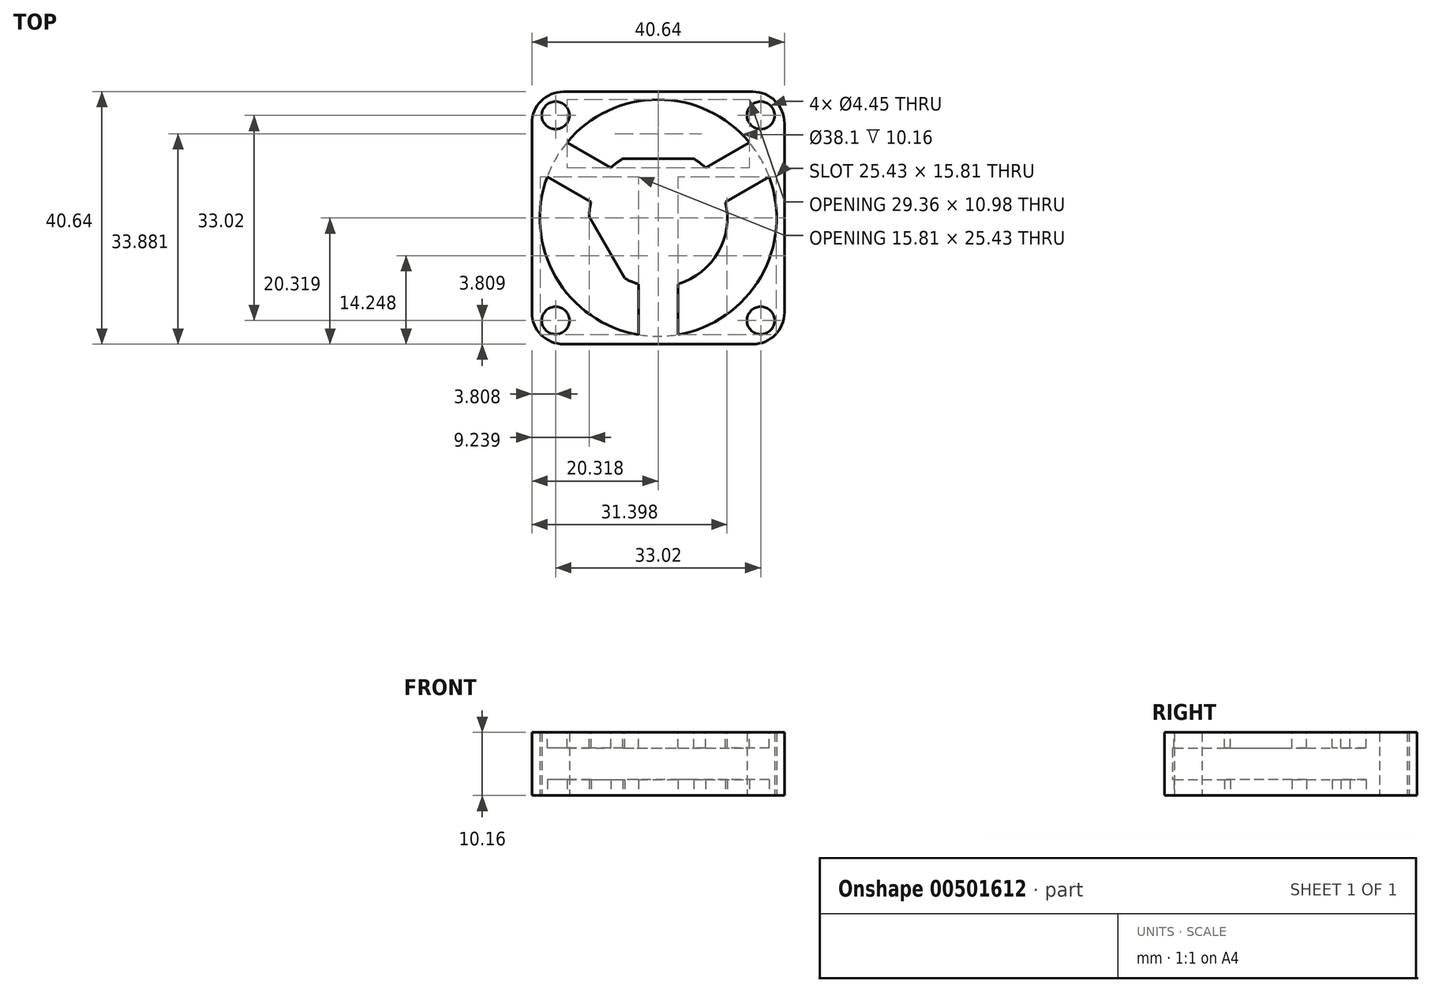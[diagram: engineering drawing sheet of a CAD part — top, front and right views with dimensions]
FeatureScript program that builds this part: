
annotation { "Feature Type Name" : "Feature", "Feature Type Description" : "" }
export const myFeature = defineFeature(function(context is Context, id is Id, definition is map)
    precondition{}
    {
        {
            var Q0;
            Q0=qCreatedBy(makeId("Top.planeOp"),FACE);
            var sketch = newSketch(context, id + "F0", { "sketchPlane" : qUnion([Q0])});
            skLineSegment(sketch, "E0.bottom", {"start": v(-69.1, 68.37) * mm, "end": v(-28.46, 68.37) * mm});
            skLineSegment(sketch, "E0.top", {"start": v(-69.1, 27.73) * mm, "end": v(-28.46, 27.73) * mm});
            skLineSegment(sketch, "E0.left", {"start": v(-69.1, 68.37) * mm, "end": v(-69.1, 27.73) * mm});
            skLineSegment(sketch, "E0.right", {"start": v(-28.46, 68.37) * mm, "end": v(-28.46, 27.73) * mm});
            skCircle(sketch, "E1", {"center": v(-65.3, 64.56) * mm, "radius": 2.22 * mm});
            skCircle(sketch, "E2", {"center": v(-32.27, 64.56) * mm, "radius": 2.22 * mm});
            skCircle(sketch, "E3", {"center": v(-65.3, 31.54) * mm, "radius": 2.22 * mm});
            skCircle(sketch, "E4", {"center": v(-32.27, 31.54) * mm, "radius": 2.22 * mm});
            skCircle(sketch, "E5", {"center": v(-48.78, 48.05) * mm, "radius": 19.05 * mm});
            skPoint(sketch, "E5.centerSnap0", {"position": v(-48.78, 68.37) * mm});
            skPoint(sketch, "E5.centerSnap1", {"position": v(-69.1, 48.05) * mm});
            skSolve(sketch);
        }
        {
            var Q0;
            Q0 = qSketchRegion(id + "F0", true);
            extrude(context, id + "F1", {"entities" : qUnion([Q0]), "depth" : 10.16 * mm});
        }
        {
            var Q0;
            Q0=makeQuery(id+"F1.opExtrude","CAP_FACE",FACE,{"disambiguationData":[OSD([sQuery(id+"F0.wireOp",EDGE,"E0.bottom"),sQuery(id+"F0.wireOp",EDGE,"E0.top"),sQuery(id+"F0.wireOp",EDGE,"E0.left"),sQuery(id+"F0.wireOp",EDGE,"E0.right"),sQuery(id+"F0.wireOp",EDGE,"E1"),sQuery(id+"F0.wireOp",EDGE,"E2"),sQuery(id+"F0.wireOp",EDGE,"E3"),sQuery(id+"F0.wireOp",EDGE,"E4"),sQuery(id+"F0.wireOp",EDGE,"E5")])],"isStart":true});
            var sketch = newSketch(context, id + "F2", { "sketchPlane" : qUnion([Q0])});
            skPoint(sketch, "E6", {"position": v(-48.78, -48.05) * mm});
            skCircle(sketch, "E7", {"center": v(-48.78, -48.05) * mm, "radius": 11.11 * mm});
            skCircle(sketch, "E8", {"center": v(-48.78, -48.05) * mm, "radius": 19.05 * mm});
            skPoint(sketch, "E9.0.midPoint", {"position": v(-48.78, -67.1) * mm});
            skCircle(sketch, "E10.cCircle", {"center": v(-48.78, -48.05) * mm, "radius": 9.53 * mm, "construction": true});
            skLineSegment(sketch, "E10.0", {"start": v(-32.28, -57.57) * mm, "end": v(-65.28, -57.57) * mm});
            skLineSegment(sketch, "E10.1", {"start": v(-65.28, -57.57) * mm, "end": v(-48.78, -29) * mm});
            skLineSegment(sketch, "E10.2", {"start": v(-48.78, -29) * mm, "end": v(-32.28, -57.57) * mm});
            skPoint(sketch, "E10.0.midPoint", {"position": v(-48.78, -57.57) * mm});
            skLineSegment(sketch, "E11", {"start": v(-65.28, -57.57) * mm, "end": v(-48.78, -48.05) * mm});
            skLineSegment(sketch, "E12", {"start": v(-32.28, -57.57) * mm, "end": v(-48.78, -48.05) * mm});
            skLineSegment(sketch, "E13", {"start": v(-48.78, -29) * mm, "end": v(-48.78, -48.05) * mm});
            skLineSegment(sketch, "E14", {"start": v(-65.28, -57.57) * mm, "end": v(-63.7, -60.32) * mm});
            skLineSegment(sketch, "E15", {"start": v(-63.7, -60.32) * mm, "end": v(-47.2, -50.8) * mm});
            skLineSegment(sketch, "E16", {"start": v(-47.2, -50.8) * mm, "end": v(-50.37, -45.3) * mm});
            skLineSegment(sketch, "E17", {"start": v(-50.37, -45.3) * mm, "end": v(-66.87, -54.82) * mm});
            skLineSegment(sketch, "E18", {"start": v(-66.87, -54.82) * mm, "end": v(-65.28, -57.57) * mm});
            skLineSegment(sketch, "E19", {"start": v(-32.28, -57.57) * mm, "end": v(-30.7, -54.82) * mm});
            skLineSegment(sketch, "E20", {"start": v(-30.7, -54.82) * mm, "end": v(-47.2, -45.3) * mm});
            skLineSegment(sketch, "E21", {"start": v(-47.2, -45.3) * mm, "end": v(-48.78, -48.05) * mm});
            skLineSegment(sketch, "E22", {"start": v(-48.78, -48.05) * mm, "end": v(-50.37, -50.8) * mm});
            skLineSegment(sketch, "E23", {"start": v(-50.37, -50.8) * mm, "end": v(-33.87, -60.32) * mm});
            skLineSegment(sketch, "E24", {"start": v(-33.87, -60.32) * mm, "end": v(-32.28, -57.57) * mm});
            skLineSegment(sketch, "E25", {"start": v(-48.78, -29) * mm, "end": v(-45.6, -29) * mm});
            skLineSegment(sketch, "E26", {"start": v(-45.6, -29) * mm, "end": v(-45.6, -48.05) * mm});
            skLineSegment(sketch, "E27", {"start": v(-45.6, -48.05) * mm, "end": v(-48.78, -48.05) * mm});
            skLineSegment(sketch, "E28", {"start": v(-48.78, -48.05) * mm, "end": v(-51.96, -48.05) * mm});
            skLineSegment(sketch, "E29", {"start": v(-51.96, -48.05) * mm, "end": v(-51.96, -29) * mm});
            skLineSegment(sketch, "E30", {"start": v(-51.96, -29) * mm, "end": v(-48.78, -29) * mm});
            skSolve(sketch);
        }
        {
            var Q0;
            {var subQ0=sQuery(id+"F2.wireOp",EDGE,"E17");var subQ1=sQuery(id+"F2.wireOp",EDGE,"E7");var subQ2=makeQuery(id+"F2.imprint","INTERSECT",VERTEX,{"derivedFrom":[subQ1,subQ0]});Q0=makeQuery(id+"F2.imprint","IMPRINT",FACE,{"disambiguationData":[TD([[makeQuery(id+"F2.imprint","IMPRINT",EDGE,{"disambiguationData":[TD([[subQ2,-1.0]])],"derivedFrom":subQ1}),-1.0]])]});}
            var Q1;
            {var subQ1=sQuery(id+"F2.wireOp",EDGE,"E8");var subQ3=sQuery(id+"F2.wireOp",EDGE,"E15");var subQ4=makeQuery(id+"F2.imprint","INTERSECT",VERTEX,{"derivedFrom":[subQ1,subQ3]});Q1=makeQuery(id+"F2.imprint","IMPRINT",FACE,{"disambiguationData":[TD([[makeQuery(id+"F2.imprint","IMPRINT",EDGE,{"disambiguationData":[TD([[subQ4,-1.0]])],"derivedFrom":subQ3}),1.0]])]});}
            var Q2;
            {var subQ0=sQuery(id+"F2.wireOp",EDGE,"E11");var subQ1=sQuery(id+"F2.wireOp",EDGE,"E7");var subQ2=makeQuery(id+"F2.imprint","INTERSECT",VERTEX,{"derivedFrom":[subQ1,subQ0]});Q2=makeQuery(id+"F2.imprint","IMPRINT",FACE,{"disambiguationData":[TD([[makeQuery(id+"F2.imprint","IMPRINT",EDGE,{"disambiguationData":[TD([[subQ2,-1.0]])],"derivedFrom":subQ1}),-1.0]])]});}
            var Q3;
            {var subQ1=sQuery(id+"F2.wireOp",EDGE,"E8");var subQ3=sQuery(id+"F2.wireOp",EDGE,"E17");var subQ4=makeQuery(id+"F2.imprint","INTERSECT",VERTEX,{"derivedFrom":[subQ1,subQ3]});Q3=makeQuery(id+"F2.imprint","IMPRINT",FACE,{"disambiguationData":[TD([[makeQuery(id+"F2.imprint","IMPRINT",EDGE,{"disambiguationData":[TD([[subQ4,1.0]])],"derivedFrom":subQ3}),1.0]])]});}
            var Q4;
            {var subQ5=sQuery(id+"F2.wireOp",EDGE,"E28");Q4=makeQuery(id+"F2.imprint","IMPRINT",FACE,{"disambiguationData":[TD([[makeQuery(id+"F2.imprint","IMPRINT",EDGE,{"derivedFrom":subQ5}),1.0]])]});}
            var Q5;
            {var subQ0=sQuery(id+"F2.wireOp",EDGE,"E22");Q5=makeQuery(id+"F2.imprint","IMPRINT",FACE,{"disambiguationData":[TD([[makeQuery(id+"F2.imprint","IMPRINT",EDGE,{"derivedFrom":subQ0}),-1.0]])]});}
            var Q6;
            {var subQ0=sQuery(id+"F2.wireOp",EDGE,"E15");var subQ1=sQuery(id+"F2.wireOp",EDGE,"E7");var subQ2=makeQuery(id+"F2.imprint","INTERSECT",VERTEX,{"derivedFrom":[subQ1,subQ0]});Q6=makeQuery(id+"F2.imprint","IMPRINT",FACE,{"disambiguationData":[TD([[makeQuery(id+"F2.imprint","IMPRINT",EDGE,{"disambiguationData":[TD([[subQ2,-1.0]])],"derivedFrom":subQ1}),1.0]])]});}
            var Q7;
            {var subQ1=sQuery(id+"F2.wireOp",EDGE,"E7");var subQ3=sQuery(id+"F2.wireOp",EDGE,"E29");var subQ8=makeQuery(id+"F2.imprint","INTERSECT",VERTEX,{"derivedFrom":[subQ1,subQ3]});Q7=makeQuery(id+"F2.imprint","IMPRINT",FACE,{"disambiguationData":[TD([[makeQuery(id+"F2.imprint","IMPRINT",EDGE,{"disambiguationData":[TD([[subQ8,-1.0]])],"derivedFrom":subQ1}),1.0]])]});}
            var Q8;
            {var subQ0=sQuery(id+"F2.wireOp",EDGE,"E28");Q8=makeQuery(id+"F2.imprint","IMPRINT",FACE,{"disambiguationData":[TD([[makeQuery(id+"F2.imprint","IMPRINT",EDGE,{"derivedFrom":subQ0}),-1.0]])]});}
            var Q9;
            {var subQ5=sQuery(id+"F2.wireOp",EDGE,"E22");Q9=makeQuery(id+"F2.imprint","IMPRINT",FACE,{"disambiguationData":[TD([[makeQuery(id+"F2.imprint","IMPRINT",EDGE,{"derivedFrom":subQ5}),1.0]])]});}
            var Q10;
            {var subQ0=sQuery(id+"F2.wireOp",EDGE,"E21");Q10=makeQuery(id+"F2.imprint","IMPRINT",FACE,{"disambiguationData":[TD([[makeQuery(id+"F2.imprint","IMPRINT",EDGE,{"derivedFrom":subQ0}),1.0]])]});}
            var Q11;
            {var subQ0=sQuery(id+"F2.wireOp",EDGE,"E21");Q11=makeQuery(id+"F2.imprint","IMPRINT",FACE,{"disambiguationData":[TD([[makeQuery(id+"F2.imprint","IMPRINT",EDGE,{"derivedFrom":subQ0}),-1.0]])]});}
            var Q12;
            {var subQ5=sQuery(id+"F2.wireOp",EDGE,"E13");var subQ7=sQuery(id+"F2.wireOp",EDGE,"E7");var subQ8=makeQuery(id+"F2.imprint","INTERSECT",VERTEX,{"derivedFrom":[subQ7,subQ5]});Q12=makeQuery(id+"F2.imprint","IMPRINT",FACE,{"disambiguationData":[TD([[makeQuery(id+"F2.imprint","IMPRINT",EDGE,{"disambiguationData":[TD([[subQ8,-1.0]])],"derivedFrom":subQ7}),1.0]])]});}
            var Q13;
            {var subQ0=sQuery(id+"F2.wireOp",EDGE,"E10.1");var subQ1=sQuery(id+"F2.wireOp",EDGE,"E7");var subQ2=makeQuery(id+"F2.imprint","INTERSECT",VERTEX,{"disambiguationData":[OD(0.0)],"derivedFrom":[subQ1,subQ0]});Q13=makeQuery(id+"F2.imprint","IMPRINT",FACE,{"disambiguationData":[TD([[makeQuery(id+"F2.imprint","IMPRINT",EDGE,{"disambiguationData":[TD([[subQ2,-1.0]])],"derivedFrom":subQ1}),1.0]])]});}
            var Q14;
            {var subQ0=sQuery(id+"F2.wireOp",EDGE,"E10.0");var subQ1=sQuery(id+"F2.wireOp",EDGE,"E7");var subQ2=makeQuery(id+"F2.imprint","INTERSECT",VERTEX,{"disambiguationData":[OD(0.0)],"derivedFrom":[subQ1,subQ0]});Q14=makeQuery(id+"F2.imprint","IMPRINT",FACE,{"disambiguationData":[TD([[makeQuery(id+"F2.imprint","IMPRINT",EDGE,{"disambiguationData":[TD([[subQ2,-1.0]])],"derivedFrom":subQ1}),1.0]])]});}
            var Q15;
            {var subQ3=sQuery(id+"F2.wireOp",EDGE,"E23");var subQ7=sQuery(id+"F2.wireOp",EDGE,"E7");var subQ9=makeQuery(id+"F2.imprint","INTERSECT",VERTEX,{"derivedFrom":[subQ7,subQ3]});Q15=makeQuery(id+"F2.imprint","IMPRINT",FACE,{"disambiguationData":[TD([[makeQuery(id+"F2.imprint","IMPRINT",EDGE,{"disambiguationData":[TD([[subQ9,-1.0]])],"derivedFrom":subQ7}),1.0]])]});}
            var Q16;
            {var subQ0=sQuery(id+"F2.wireOp",EDGE,"E27");Q16=makeQuery(id+"F2.imprint","IMPRINT",FACE,{"disambiguationData":[TD([[makeQuery(id+"F2.imprint","IMPRINT",EDGE,{"derivedFrom":subQ0}),1.0]])]});}
            var Q17;
            {var subQ0=sQuery(id+"F2.wireOp",EDGE,"E23");var subQ1=sQuery(id+"F2.wireOp",EDGE,"E7");var subQ2=makeQuery(id+"F2.imprint","INTERSECT",VERTEX,{"derivedFrom":[subQ1,subQ0]});Q17=makeQuery(id+"F2.imprint","IMPRINT",FACE,{"disambiguationData":[TD([[makeQuery(id+"F2.imprint","IMPRINT",EDGE,{"disambiguationData":[TD([[subQ2,-1.0]])],"derivedFrom":subQ1}),-1.0]])]});}
            var Q18;
            {var subQ1=sQuery(id+"F2.wireOp",EDGE,"E8");var subQ3=sQuery(id+"F2.wireOp",EDGE,"E23");var subQ4=makeQuery(id+"F2.imprint","INTERSECT",VERTEX,{"derivedFrom":[subQ1,subQ3]});Q18=makeQuery(id+"F2.imprint","IMPRINT",FACE,{"disambiguationData":[TD([[makeQuery(id+"F2.imprint","IMPRINT",EDGE,{"disambiguationData":[TD([[subQ4,1.0]])],"derivedFrom":subQ3}),1.0]])]});}
            var Q19;
            {var subQ1=sQuery(id+"F2.wireOp",EDGE,"E8");var subQ3=sQuery(id+"F2.wireOp",EDGE,"E20");var subQ4=makeQuery(id+"F2.imprint","INTERSECT",VERTEX,{"derivedFrom":[subQ1,subQ3]});Q19=makeQuery(id+"F2.imprint","IMPRINT",FACE,{"disambiguationData":[TD([[makeQuery(id+"F2.imprint","IMPRINT",EDGE,{"disambiguationData":[TD([[subQ4,-1.0]])],"derivedFrom":subQ3}),1.0]])]});}
            var Q20;
            {var subQ0=sQuery(id+"F2.wireOp",EDGE,"E12");var subQ1=sQuery(id+"F2.wireOp",EDGE,"E7");var subQ2=makeQuery(id+"F2.imprint","INTERSECT",VERTEX,{"derivedFrom":[subQ1,subQ0]});Q20=makeQuery(id+"F2.imprint","IMPRINT",FACE,{"disambiguationData":[TD([[makeQuery(id+"F2.imprint","IMPRINT",EDGE,{"disambiguationData":[TD([[subQ2,-1.0]])],"derivedFrom":subQ1}),-1.0]])]});}
            var Q21;
            {var subQ1=sQuery(id+"F2.wireOp",EDGE,"E7");var subQ6=sQuery(id+"F2.wireOp",EDGE,"E26");var subQ8=makeQuery(id+"F2.imprint","INTERSECT",VERTEX,{"derivedFrom":[subQ1,subQ6]});Q21=makeQuery(id+"F2.imprint","IMPRINT",FACE,{"disambiguationData":[TD([[makeQuery(id+"F2.imprint","IMPRINT",EDGE,{"disambiguationData":[TD([[subQ8,1.0]])],"derivedFrom":subQ1}),1.0]])]});}
            var Q22;
            {var subQ0=sQuery(id+"F2.wireOp",EDGE,"E10.2");var subQ1=sQuery(id+"F2.wireOp",EDGE,"E7");var subQ2=makeQuery(id+"F2.imprint","INTERSECT",VERTEX,{"disambiguationData":[OD(0.0)],"derivedFrom":[subQ1,subQ0]});Q22=makeQuery(id+"F2.imprint","IMPRINT",FACE,{"disambiguationData":[TD([[makeQuery(id+"F2.imprint","IMPRINT",EDGE,{"disambiguationData":[TD([[subQ2,1.0]])],"derivedFrom":subQ1}),1.0]])]});}
            var Q23;
            {var subQ0=sQuery(id+"F2.wireOp",EDGE,"E13");var subQ1=sQuery(id+"F2.wireOp",EDGE,"E7");var subQ2=makeQuery(id+"F2.imprint","INTERSECT",VERTEX,{"derivedFrom":[subQ1,subQ0]});Q23=makeQuery(id+"F2.imprint","IMPRINT",FACE,{"disambiguationData":[TD([[makeQuery(id+"F2.imprint","IMPRINT",EDGE,{"disambiguationData":[TD([[subQ2,-1.0]])],"derivedFrom":subQ1}),-1.0]])]});}
            var Q24;
            {var subQ1=sQuery(id+"F2.wireOp",EDGE,"E8");var subQ3=sQuery(id+"F2.wireOp",EDGE,"E29");var subQ4=makeQuery(id+"F2.imprint","INTERSECT",VERTEX,{"derivedFrom":[subQ1,subQ3]});Q24=makeQuery(id+"F2.imprint","IMPRINT",FACE,{"disambiguationData":[TD([[makeQuery(id+"F2.imprint","IMPRINT",EDGE,{"disambiguationData":[TD([[subQ4,1.0]])],"derivedFrom":subQ3}),-1.0]])]});}
            var Q25;
            {var subQ0=sQuery(id+"F2.wireOp",EDGE,"E26");var subQ1=sQuery(id+"F2.wireOp",EDGE,"E7");var subQ2=makeQuery(id+"F2.imprint","INTERSECT",VERTEX,{"derivedFrom":[subQ1,subQ0]});Q25=makeQuery(id+"F2.imprint","IMPRINT",FACE,{"disambiguationData":[TD([[makeQuery(id+"F2.imprint","IMPRINT",EDGE,{"disambiguationData":[TD([[subQ2,-1.0]])],"derivedFrom":subQ1}),-1.0]])]});}
            var Q26;
            {var subQ1=sQuery(id+"F2.wireOp",EDGE,"E8");var subQ3=sQuery(id+"F2.wireOp",EDGE,"E26");var subQ4=makeQuery(id+"F2.imprint","INTERSECT",VERTEX,{"derivedFrom":[subQ1,subQ3]});Q26=makeQuery(id+"F2.imprint","IMPRINT",FACE,{"disambiguationData":[TD([[makeQuery(id+"F2.imprint","IMPRINT",EDGE,{"disambiguationData":[TD([[subQ4,-1.0]])],"derivedFrom":subQ3}),-1.0]])]});}
            extrude(context, id + "F3", {"entities" : qUnion([Q0, Q1, Q2, Q3, Q4, Q5, Q6, Q7, Q8, Q9, Q10, Q11, Q12, Q13, Q14, Q15, Q16, Q17, Q18, Q19, Q20, Q21, Q22, Q23, Q24, Q25, Q26]), "operationType" : NewBodyOperationType.ADD, "oppositeDirection" : true, "depth" : 2.54 * mm});
        }
        {
            var Q0;
            Q0=makeQuery(id+"F1.opExtrude","CAP_FACE",FACE,{"disambiguationData":[OSD([sQuery(id+"F0.wireOp",EDGE,"E0.bottom"),sQuery(id+"F0.wireOp",EDGE,"E0.top"),sQuery(id+"F0.wireOp",EDGE,"E0.left"),sQuery(id+"F0.wireOp",EDGE,"E0.right"),sQuery(id+"F0.wireOp",EDGE,"E1"),sQuery(id+"F0.wireOp",EDGE,"E2"),sQuery(id+"F0.wireOp",EDGE,"E3"),sQuery(id+"F0.wireOp",EDGE,"E4"),sQuery(id+"F0.wireOp",EDGE,"E5")])],"isStart":false});
            var sketch = newSketch(context, id + "F4", { "sketchPlane" : qUnion([Q0])});
            skCircle(sketch, "E31", {"center": v(-48.78, 48.05) * mm, "radius": 11.11 * mm});
            skCircle(sketch, "E32", {"center": v(-48.78, 48.05) * mm, "radius": 19.05 * mm});
            skCircle(sketch, "E33.cCircle", {"center": v(-48.78, 48.05) * mm, "radius": 9.53 * mm, "construction": true});
            skLineSegment(sketch, "E33.0", {"start": v(-65.28, 57.57) * mm, "end": v(-32.28, 57.57) * mm});
            skLineSegment(sketch, "E33.1", {"start": v(-32.28, 57.57) * mm, "end": v(-48.78, 29) * mm});
            skLineSegment(sketch, "E33.2", {"start": v(-48.78, 29) * mm, "end": v(-65.28, 57.57) * mm});
            skPoint(sketch, "E33.0.midPoint", {"position": v(-48.78, 57.57) * mm});
            skLineSegment(sketch, "E34", {"start": v(-65.28, 57.57) * mm, "end": v(-48.78, 48.05) * mm});
            skLineSegment(sketch, "E35", {"start": v(-32.28, 57.57) * mm, "end": v(-48.78, 48.05) * mm});
            skLineSegment(sketch, "E36", {"start": v(-48.78, 29) * mm, "end": v(-48.78, 48.05) * mm});
            skLineSegment(sketch, "E37", {"start": v(-65.28, 57.57) * mm, "end": v(-63.7, 60.32) * mm});
            skLineSegment(sketch, "E38", {"start": v(-63.7, 60.32) * mm, "end": v(-47.2, 50.8) * mm});
            skLineSegment(sketch, "E39", {"start": v(-47.2, 50.8) * mm, "end": v(-48.78, 48.05) * mm});
            skLineSegment(sketch, "E40", {"start": v(-48.78, 48.05) * mm, "end": v(-50.37, 45.3) * mm});
            skLineSegment(sketch, "E41", {"start": v(-50.37, 45.3) * mm, "end": v(-66.87, 54.82) * mm});
            skLineSegment(sketch, "E42", {"start": v(-66.87, 54.82) * mm, "end": v(-65.28, 57.57) * mm});
            skLineSegment(sketch, "E43", {"start": v(-32.28, 57.57) * mm, "end": v(-30.7, 54.82) * mm});
            skLineSegment(sketch, "E44", {"start": v(-30.7, 54.82) * mm, "end": v(-47.2, 45.3) * mm});
            skLineSegment(sketch, "E45", {"start": v(-47.2, 45.3) * mm, "end": v(-48.78, 48.05) * mm});
            skLineSegment(sketch, "E46", {"start": v(-48.78, 48.05) * mm, "end": v(-50.37, 50.8) * mm});
            skLineSegment(sketch, "E47", {"start": v(-50.37, 50.8) * mm, "end": v(-33.87, 60.32) * mm});
            skLineSegment(sketch, "E48", {"start": v(-33.87, 60.32) * mm, "end": v(-32.28, 57.57) * mm});
            skLineSegment(sketch, "E49", {"start": v(-48.78, 29) * mm, "end": v(-51.96, 29) * mm});
            skLineSegment(sketch, "E50", {"start": v(-51.96, 29) * mm, "end": v(-51.96, 48.05) * mm});
            skLineSegment(sketch, "E51", {"start": v(-51.96, 48.05) * mm, "end": v(-48.78, 48.05) * mm});
            skLineSegment(sketch, "E52", {"start": v(-48.78, 48.05) * mm, "end": v(-45.6, 48.05) * mm});
            skLineSegment(sketch, "E53", {"start": v(-45.6, 48.05) * mm, "end": v(-45.6, 29) * mm});
            skLineSegment(sketch, "E54", {"start": v(-45.6, 29) * mm, "end": v(-48.78, 29) * mm});
            skSolve(sketch);
        }
        {
            var Q0;
            {var subQ1=sQuery(id+"F4.wireOp",EDGE,"E32");var subQ3=sQuery(id+"F4.wireOp",EDGE,"E41");var subQ4=makeQuery(id+"F4.imprint","INTERSECT",VERTEX,{"derivedFrom":[subQ1,subQ3]});Q0=makeQuery(id+"F4.imprint","IMPRINT",FACE,{"disambiguationData":[TD([[makeQuery(id+"F4.imprint","IMPRINT",EDGE,{"disambiguationData":[TD([[subQ4,1.0]])],"derivedFrom":subQ3}),-1.0]])]});}
            var Q1;
            {var subQ0=sQuery(id+"F4.wireOp",EDGE,"E34");var subQ1=sQuery(id+"F4.wireOp",EDGE,"E31");var subQ2=makeQuery(id+"F4.imprint","INTERSECT",VERTEX,{"derivedFrom":[subQ1,subQ0]});Q1=makeQuery(id+"F4.imprint","IMPRINT",FACE,{"disambiguationData":[TD([[makeQuery(id+"F4.imprint","IMPRINT",EDGE,{"disambiguationData":[TD([[subQ2,-1.0]])],"derivedFrom":subQ1}),-1.0]])]});}
            var Q2;
            {var subQ0=sQuery(id+"F4.wireOp",EDGE,"E38");var subQ1=sQuery(id+"F4.wireOp",EDGE,"E31");var subQ2=makeQuery(id+"F4.imprint","INTERSECT",VERTEX,{"derivedFrom":[subQ1,subQ0]});Q2=makeQuery(id+"F4.imprint","IMPRINT",FACE,{"disambiguationData":[TD([[makeQuery(id+"F4.imprint","IMPRINT",EDGE,{"disambiguationData":[TD([[subQ2,-1.0]])],"derivedFrom":subQ1}),-1.0]])]});}
            var Q3;
            {var subQ1=sQuery(id+"F4.wireOp",EDGE,"E32");var subQ3=sQuery(id+"F4.wireOp",EDGE,"E38");var subQ4=makeQuery(id+"F4.imprint","INTERSECT",VERTEX,{"derivedFrom":[subQ1,subQ3]});Q3=makeQuery(id+"F4.imprint","IMPRINT",FACE,{"disambiguationData":[TD([[makeQuery(id+"F4.imprint","IMPRINT",EDGE,{"disambiguationData":[TD([[subQ4,-1.0]])],"derivedFrom":subQ3}),-1.0]])]});}
            var Q4;
            {var subQ1=sQuery(id+"F4.wireOp",EDGE,"E31");var subQ3=sQuery(id+"F4.wireOp",EDGE,"E47");var subQ8=makeQuery(id+"F4.imprint","INTERSECT",VERTEX,{"derivedFrom":[subQ1,subQ3]});Q4=makeQuery(id+"F4.imprint","IMPRINT",FACE,{"disambiguationData":[TD([[makeQuery(id+"F4.imprint","IMPRINT",EDGE,{"disambiguationData":[TD([[subQ8,-1.0]])],"derivedFrom":subQ1}),1.0]])]});}
            var Q5;
            {var subQ0=sQuery(id+"F4.wireOp",EDGE,"E33.0");var subQ1=sQuery(id+"F4.wireOp",EDGE,"E31");var subQ2=makeQuery(id+"F4.imprint","INTERSECT",VERTEX,{"disambiguationData":[OD(0.0)],"derivedFrom":[subQ1,subQ0]});Q5=makeQuery(id+"F4.imprint","IMPRINT",FACE,{"disambiguationData":[TD([[makeQuery(id+"F4.imprint","IMPRINT",EDGE,{"disambiguationData":[TD([[subQ2,-1.0]])],"derivedFrom":subQ1}),1.0]])]});}
            var Q6;
            {var subQ5=sQuery(id+"F4.wireOp",EDGE,"E46");Q6=makeQuery(id+"F4.imprint","IMPRINT",FACE,{"disambiguationData":[TD([[makeQuery(id+"F4.imprint","IMPRINT",EDGE,{"derivedFrom":subQ5}),1.0]])]});}
            var Q7;
            {var subQ0=sQuery(id+"F4.wireOp",EDGE,"E51");Q7=makeQuery(id+"F4.imprint","IMPRINT",FACE,{"disambiguationData":[TD([[makeQuery(id+"F4.imprint","IMPRINT",EDGE,{"derivedFrom":subQ0}),1.0]])]});}
            var Q8;
            {var subQ0=sQuery(id+"F4.wireOp",EDGE,"E33.2");var subQ1=sQuery(id+"F4.wireOp",EDGE,"E31");var subQ2=makeQuery(id+"F4.imprint","INTERSECT",VERTEX,{"disambiguationData":[OD(0.0)],"derivedFrom":[subQ1,subQ0]});Q8=makeQuery(id+"F4.imprint","IMPRINT",FACE,{"disambiguationData":[TD([[makeQuery(id+"F4.imprint","IMPRINT",EDGE,{"disambiguationData":[TD([[subQ2,-1.0]])],"derivedFrom":subQ1}),1.0]])]});}
            var Q9;
            {var subQ0=sQuery(id+"F4.wireOp",EDGE,"E41");var subQ1=sQuery(id+"F4.wireOp",EDGE,"E31");var subQ2=makeQuery(id+"F4.imprint","INTERSECT",VERTEX,{"derivedFrom":[subQ1,subQ0]});Q9=makeQuery(id+"F4.imprint","IMPRINT",FACE,{"disambiguationData":[TD([[makeQuery(id+"F4.imprint","IMPRINT",EDGE,{"disambiguationData":[TD([[subQ2,-1.0]])],"derivedFrom":subQ1}),1.0]])]});}
            var Q10;
            {var subQ1=sQuery(id+"F4.wireOp",EDGE,"E40");Q10=makeQuery(id+"F4.imprint","IMPRINT",FACE,{"disambiguationData":[TD([[makeQuery(id+"F4.imprint","IMPRINT",EDGE,{"derivedFrom":subQ1}),1.0]])]});}
            var Q11;
            {var subQ0=sQuery(id+"F4.wireOp",EDGE,"E45");Q11=makeQuery(id+"F4.imprint","IMPRINT",FACE,{"disambiguationData":[TD([[makeQuery(id+"F4.imprint","IMPRINT",EDGE,{"derivedFrom":subQ0}),1.0]])]});}
            var Q12;
            {var subQ0=sQuery(id+"F4.wireOp",EDGE,"E40");Q12=makeQuery(id+"F4.imprint","IMPRINT",FACE,{"disambiguationData":[TD([[makeQuery(id+"F4.imprint","IMPRINT",EDGE,{"derivedFrom":subQ0}),-1.0]])]});}
            var Q13;
            {var subQ0=sQuery(id+"F4.wireOp",EDGE,"E39");Q13=makeQuery(id+"F4.imprint","IMPRINT",FACE,{"disambiguationData":[TD([[makeQuery(id+"F4.imprint","IMPRINT",EDGE,{"derivedFrom":subQ0}),1.0]])]});}
            var Q14;
            {var subQ0=sQuery(id+"F4.wireOp",EDGE,"E52");Q14=makeQuery(id+"F4.imprint","IMPRINT",FACE,{"disambiguationData":[TD([[makeQuery(id+"F4.imprint","IMPRINT",EDGE,{"derivedFrom":subQ0}),1.0]])]});}
            var Q15;
            {var subQ0=sQuery(id+"F4.wireOp",EDGE,"E45");Q15=makeQuery(id+"F4.imprint","IMPRINT",FACE,{"disambiguationData":[TD([[makeQuery(id+"F4.imprint","IMPRINT",EDGE,{"derivedFrom":subQ0}),-1.0]])]});}
            var Q16;
            {var subQ0=sQuery(id+"F4.wireOp",EDGE,"E39");Q16=makeQuery(id+"F4.imprint","IMPRINT",FACE,{"disambiguationData":[TD([[makeQuery(id+"F4.imprint","IMPRINT",EDGE,{"derivedFrom":subQ0}),-1.0]])]});}
            var Q17;
            {var subQ1=sQuery(id+"F4.wireOp",EDGE,"E32");var subQ3=sQuery(id+"F4.wireOp",EDGE,"E47");var subQ4=makeQuery(id+"F4.imprint","INTERSECT",VERTEX,{"derivedFrom":[subQ1,subQ3]});Q17=makeQuery(id+"F4.imprint","IMPRINT",FACE,{"disambiguationData":[TD([[makeQuery(id+"F4.imprint","IMPRINT",EDGE,{"disambiguationData":[TD([[subQ4,1.0]])],"derivedFrom":subQ3}),-1.0]])]});}
            var Q18;
            {var subQ0=sQuery(id+"F4.wireOp",EDGE,"E35");var subQ1=sQuery(id+"F4.wireOp",EDGE,"E31");var subQ2=makeQuery(id+"F4.imprint","INTERSECT",VERTEX,{"derivedFrom":[subQ1,subQ0]});Q18=makeQuery(id+"F4.imprint","IMPRINT",FACE,{"disambiguationData":[TD([[makeQuery(id+"F4.imprint","IMPRINT",EDGE,{"disambiguationData":[TD([[subQ2,-1.0]])],"derivedFrom":subQ1}),-1.0]])]});}
            var Q19;
            {var subQ0=sQuery(id+"F4.wireOp",EDGE,"E44");var subQ1=sQuery(id+"F4.wireOp",EDGE,"E31");var subQ2=makeQuery(id+"F4.imprint","INTERSECT",VERTEX,{"derivedFrom":[subQ1,subQ0]});Q19=makeQuery(id+"F4.imprint","IMPRINT",FACE,{"disambiguationData":[TD([[makeQuery(id+"F4.imprint","IMPRINT",EDGE,{"disambiguationData":[TD([[subQ2,-1.0]])],"derivedFrom":subQ1}),-1.0]])]});}
            var Q20;
            {var subQ1=sQuery(id+"F4.wireOp",EDGE,"E32");var subQ3=sQuery(id+"F4.wireOp",EDGE,"E44");var subQ4=makeQuery(id+"F4.imprint","INTERSECT",VERTEX,{"derivedFrom":[subQ1,subQ3]});Q20=makeQuery(id+"F4.imprint","IMPRINT",FACE,{"disambiguationData":[TD([[makeQuery(id+"F4.imprint","IMPRINT",EDGE,{"disambiguationData":[TD([[subQ4,-1.0]])],"derivedFrom":subQ3}),-1.0]])]});}
            var Q21;
            {var subQ1=sQuery(id+"F4.wireOp",EDGE,"E31");var subQ4=sQuery(id+"F4.wireOp",EDGE,"E44");var subQ5=makeQuery(id+"F4.imprint","INTERSECT",VERTEX,{"derivedFrom":[subQ1,subQ4]});Q21=makeQuery(id+"F4.imprint","IMPRINT",FACE,{"disambiguationData":[TD([[makeQuery(id+"F4.imprint","IMPRINT",EDGE,{"disambiguationData":[TD([[subQ5,1.0]])],"derivedFrom":subQ1}),1.0]])]});}
            var Q22;
            {var subQ0=sQuery(id+"F4.wireOp",EDGE,"E33.1");var subQ1=sQuery(id+"F4.wireOp",EDGE,"E31");var subQ2=makeQuery(id+"F4.imprint","INTERSECT",VERTEX,{"disambiguationData":[OD(0.0)],"derivedFrom":[subQ1,subQ0]});Q22=makeQuery(id+"F4.imprint","IMPRINT",FACE,{"disambiguationData":[TD([[makeQuery(id+"F4.imprint","IMPRINT",EDGE,{"disambiguationData":[TD([[subQ2,1.0]])],"derivedFrom":subQ1}),1.0]])]});}
            var Q23;
            {var subQ0=sQuery(id+"F4.wireOp",EDGE,"E36");var subQ1=sQuery(id+"F4.wireOp",EDGE,"E31");var subQ2=makeQuery(id+"F4.imprint","INTERSECT",VERTEX,{"derivedFrom":[subQ1,subQ0]});Q23=makeQuery(id+"F4.imprint","IMPRINT",FACE,{"disambiguationData":[TD([[makeQuery(id+"F4.imprint","IMPRINT",EDGE,{"disambiguationData":[TD([[subQ2,-1.0]])],"derivedFrom":subQ1}),-1.0]])]});}
            var Q24;
            {var subQ0=sQuery(id+"F4.wireOp",EDGE,"E50");var subQ1=sQuery(id+"F4.wireOp",EDGE,"E31");var subQ2=makeQuery(id+"F4.imprint","INTERSECT",VERTEX,{"derivedFrom":[subQ1,subQ0]});Q24=makeQuery(id+"F4.imprint","IMPRINT",FACE,{"disambiguationData":[TD([[makeQuery(id+"F4.imprint","IMPRINT",EDGE,{"disambiguationData":[TD([[subQ2,-1.0]])],"derivedFrom":subQ1}),-1.0]])]});}
            var Q25;
            {var subQ1=sQuery(id+"F4.wireOp",EDGE,"E32");var subQ3=sQuery(id+"F4.wireOp",EDGE,"E50");var subQ4=makeQuery(id+"F4.imprint","INTERSECT",VERTEX,{"derivedFrom":[subQ1,subQ3]});Q25=makeQuery(id+"F4.imprint","IMPRINT",FACE,{"disambiguationData":[TD([[makeQuery(id+"F4.imprint","IMPRINT",EDGE,{"disambiguationData":[TD([[subQ4,-1.0]])],"derivedFrom":subQ3}),-1.0]])]});}
            var Q26;
            {var subQ1=sQuery(id+"F4.wireOp",EDGE,"E32");var subQ3=sQuery(id+"F4.wireOp",EDGE,"E53");var subQ4=makeQuery(id+"F4.imprint","INTERSECT",VERTEX,{"derivedFrom":[subQ1,subQ3]});Q26=makeQuery(id+"F4.imprint","IMPRINT",FACE,{"disambiguationData":[TD([[makeQuery(id+"F4.imprint","IMPRINT",EDGE,{"disambiguationData":[TD([[subQ4,1.0]])],"derivedFrom":subQ3}),-1.0]])]});}
            extrude(context, id + "F5", {"entities" : qUnion([Q0, Q1, Q2, Q3, Q4, Q5, Q6, Q7, Q8, Q9, Q10, Q11, Q12, Q13, Q14, Q15, Q16, Q17, Q18, Q19, Q20, Q21, Q22, Q23, Q24, Q25, Q26]), "operationType" : NewBodyOperationType.ADD, "oppositeDirection" : true, "depth" : 2.54 * mm});
        }
        {
            var Q0;
            Q0=makeQuery(id+"F1.opExtrude","SWEPT_EDGE",EDGE,{"disambiguationData":[OSD([sQuery(id+"F0.wireOp",EDGE,"E0.bottom"),sQuery(id+"F0.wireOp",EDGE,"E0.left")])]});
            fillet(context, id + "F6", {"entities" : qUnion([Q0]), "radius" : 5.08 * mm, "tangentPropagation" : true, "allowEdgeOverflow" : false});
        }
        {
            var Q0;
            Q0=makeQuery(id+"F1.opExtrude","SWEPT_EDGE",EDGE,{"disambiguationData":[OSD([sQuery(id+"F0.wireOp",EDGE,"E0.bottom"),sQuery(id+"F0.wireOp",EDGE,"E0.right")])]});
            fillet(context, id + "F7", {"entities" : qUnion([Q0]), "radius" : 5.08 * mm, "tangentPropagation" : true, "allowEdgeOverflow" : false});
        }
        {
            var Q0;
            Q0=makeQuery(id+"F1.opExtrude","SWEPT_EDGE",EDGE,{"disambiguationData":[OSD([sQuery(id+"F0.wireOp",EDGE,"E0.top"),sQuery(id+"F0.wireOp",EDGE,"E0.left")])]});
            fillet(context, id + "F8", {"entities" : qUnion([Q0]), "radius" : 5.08 * mm, "tangentPropagation" : true, "allowEdgeOverflow" : false});
        }
        {
            var Q0;
            Q0=makeQuery(id+"F1.opExtrude","SWEPT_EDGE",EDGE,{"disambiguationData":[OSD([sQuery(id+"F0.wireOp",EDGE,"E0.top"),sQuery(id+"F0.wireOp",EDGE,"E0.right")])]});
            fillet(context, id + "F9", {"entities" : qUnion([Q0]), "radius" : 5.08 * mm, "tangentPropagation" : true, "allowEdgeOverflow" : false});
        }
    });
